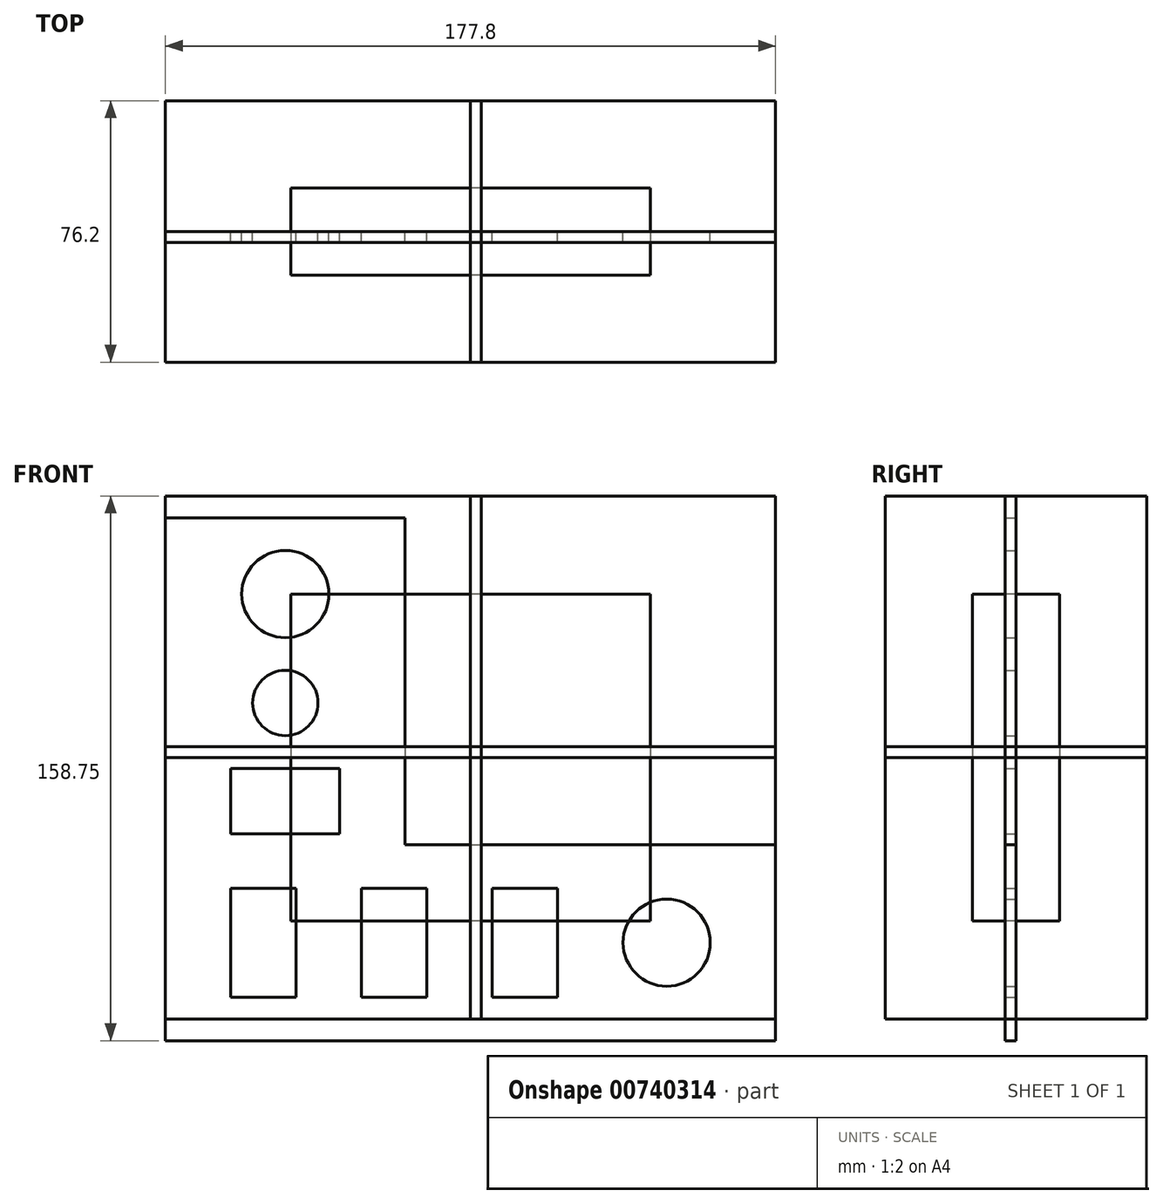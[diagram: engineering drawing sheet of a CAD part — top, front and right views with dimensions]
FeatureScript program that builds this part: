
annotation { "Feature Type Name" : "Feature", "Feature Type Description" : "" }
export const myFeature = defineFeature(function(context is Context, id is Id, definition is map)
    precondition{}
    {
        {
            var Q0;
            Q0=qCreatedBy(makeId("Front.planeOp"),FACE);
            var sketch = newSketch(context, id + "F0", { "sketchPlane" : qUnion([Q0])});
            skLineSegment(sketch, "E0.bottom", {"start": v(-19.05, 69.85) * mm, "end": v(-88.9, 69.85) * mm});
            skLineSegment(sketch, "E0.left", {"start": v(88.9, -25.4) * mm, "end": v(88.9, -69.85) * mm});
            skLineSegment(sketch, "E0.right", {"start": v(-88.9, 69.85) * mm, "end": v(-88.9, -69.85) * mm});
            skPoint(sketch, "E0.middle", {"position": v(0, 0) * mm});
            skLineSegment(sketch, "E1", {"start": v(-19.05, 69.85) * mm, "end": v(-19.05, -25.4) * mm});
            skLineSegment(sketch, "E2", {"start": v(-19.05, -25.4) * mm, "end": v(88.9, -25.4) * mm});
            skPoint(sketch, "E2.endSnap0", {"position": v(88.9, 0) * mm});
            skPoint(sketch, "E3.start.orphan", {"position": v(88.9, 69.85) * mm});
            skCircle(sketch, "E4", {"center": v(-53.98, 47.63) * mm, "radius": 12.7 * mm});
            skCircle(sketch, "E5", {"center": v(-53.98, 15.88) * mm, "radius": 9.53 * mm});
            skLineSegment(sketch, "E6.bottom", {"start": v(-38.1, -3.17) * mm, "end": v(-69.85, -3.17) * mm});
            skLineSegment(sketch, "E6.top", {"start": v(-38.1, -22.22) * mm, "end": v(-69.85, -22.22) * mm});
            skLineSegment(sketch, "E6.left", {"start": v(-38.1, -3.17) * mm, "end": v(-38.1, -22.22) * mm});
            skLineSegment(sketch, "E6.right", {"start": v(-69.85, -3.17) * mm, "end": v(-69.85, -22.22) * mm});
            skPoint(sketch, "E6.middle", {"position": v(-53.98, -12.7) * mm});
            skPoint(sketch, "E7.start.orphan", {"position": v(-53.97, 69.85) * mm});
            skLineSegment(sketch, "E8.bottom", {"start": v(-50.8, -38.1) * mm, "end": v(-69.85, -38.1) * mm});
            skLineSegment(sketch, "E8.top", {"start": v(-50.8, -69.85) * mm, "end": v(-69.85, -69.85) * mm});
            skLineSegment(sketch, "E8.left", {"start": v(-50.8, -38.1) * mm, "end": v(-50.8, -69.85) * mm});
            skLineSegment(sketch, "E8.right", {"start": v(-69.85, -38.1) * mm, "end": v(-69.85, -69.85) * mm});
            skPoint(sketch, "E8.middle", {"position": v(-60.32, -53.98) * mm});
            skLineSegment(sketch, "E9.bottom", {"start": v(-12.7, -38.1) * mm, "end": v(-31.75, -38.1) * mm});
            skLineSegment(sketch, "E9.top", {"start": v(-12.7, -69.85) * mm, "end": v(-31.75, -69.85) * mm});
            skLineSegment(sketch, "E9.left", {"start": v(-12.7, -38.1) * mm, "end": v(-12.7, -69.85) * mm});
            skLineSegment(sketch, "E9.right", {"start": v(-31.75, -38.1) * mm, "end": v(-31.75, -69.85) * mm});
            skPoint(sketch, "E9.middle", {"position": v(-22.22, -53.98) * mm});
            skLineSegment(sketch, "E10.bottom", {"start": v(25.4, -38.1) * mm, "end": v(6.35, -38.1) * mm});
            skLineSegment(sketch, "E10.top", {"start": v(25.4, -69.85) * mm, "end": v(6.35, -69.85) * mm});
            skLineSegment(sketch, "E10.left", {"start": v(25.4, -38.1) * mm, "end": v(25.4, -69.85) * mm});
            skLineSegment(sketch, "E10.right", {"start": v(6.35, -38.1) * mm, "end": v(6.35, -69.85) * mm});
            skPoint(sketch, "E10.middle", {"position": v(15.88, -53.98) * mm});
            skCircle(sketch, "E11", {"center": v(57.15, -53.98) * mm, "radius": 12.7 * mm});
            skPoint(sketch, "E12.orphan", {"position": v(88.9, -47.63) * mm});
            skLineSegment(sketch, "E13", {"start": v(88.9, -47.63) * mm, "end": v(88.9, -82.55) * mm});
            skLineSegment(sketch, "E14", {"start": v(88.9, -82.55) * mm, "end": v(-88.9, -82.55) * mm});
            skLineSegment(sketch, "E15", {"start": v(-88.9, -69.85) * mm, "end": v(-88.9, -82.55) * mm});
            skSolve(sketch);
        }
        {
            var Q0;
            Q0=qCreatedBy(makeId("Front.planeOp"),FACE);
            var sketch = newSketch(context, id + "F1", { "sketchPlane" : qUnion([Q0])});
            skLineSegment(sketch, "E16.bottom", {"start": v(52.39, 47.62) * mm, "end": v(-52.39, 47.62) * mm});
            skLineSegment(sketch, "E16.top", {"start": v(52.39, -47.63) * mm, "end": v(-52.39, -47.63) * mm});
            skLineSegment(sketch, "E16.left", {"start": v(52.39, 47.62) * mm, "end": v(52.39, -47.63) * mm});
            skLineSegment(sketch, "E16.right", {"start": v(-52.39, 47.62) * mm, "end": v(-52.39, -47.63) * mm});
            skPoint(sketch, "E16.middle", {"position": v(0, 0) * mm});
            skSolve(sketch);
        }
        {
            var Q0;
            Q0=qCreatedBy(makeId("Right.planeOp"),FACE);
            var sketch = newSketch(context, id + "F2", { "sketchPlane" : qUnion([Q0])});
            skLineSegment(sketch, "E17.bottom", {"start": v(38.1, 76.2) * mm, "end": v(-38.1, 76.2) * mm});
            skLineSegment(sketch, "E17.top", {"start": v(38.1, -76.2) * mm, "end": v(-38.1, -76.2) * mm});
            skLineSegment(sketch, "E17.left", {"start": v(38.1, 76.2) * mm, "end": v(38.1, -76.2) * mm});
            skLineSegment(sketch, "E17.right", {"start": v(-38.1, 76.2) * mm, "end": v(-38.1, -76.2) * mm});
            skPoint(sketch, "E17.middle", {"position": v(0, 0) * mm});
            skSolve(sketch);
        }
        {
            var Q0;
            Q0=qCreatedBy(makeId("Top.planeOp"),FACE);
            var sketch = newSketch(context, id + "F3", { "sketchPlane" : qUnion([Q0])});
            skLineSegment(sketch, "E18.bottom", {"start": v(88.9, 38.1) * mm, "end": v(-88.9, 38.1) * mm});
            skLineSegment(sketch, "E18.top", {"start": v(88.9, -38.1) * mm, "end": v(-88.9, -38.1) * mm});
            skLineSegment(sketch, "E18.left", {"start": v(88.9, 38.1) * mm, "end": v(88.9, -38.1) * mm});
            skLineSegment(sketch, "E18.right", {"start": v(-88.9, 38.1) * mm, "end": v(-88.9, -38.1) * mm});
            skPoint(sketch, "E18.middle", {"position": v(0, 0) * mm});
            skSolve(sketch);
        }
        {
            var Q0;
            Q0=qCreatedBy(makeId("Front.planeOp"),FACE);
            var sketch = newSketch(context, id + "F4", { "sketchPlane" : qUnion([Q0])});
            skLineSegment(sketch, "E19.bottom", {"start": v(88.9, 76.2) * mm, "end": v(-88.9, 76.2) * mm});
            skLineSegment(sketch, "E19.top", {"start": v(88.9, -76.2) * mm, "end": v(-88.9, -76.2) * mm});
            skLineSegment(sketch, "E19.left", {"start": v(88.9, 76.2) * mm, "end": v(88.9, -76.2) * mm});
            skLineSegment(sketch, "E19.right", {"start": v(-88.9, 76.2) * mm, "end": v(-88.9, -76.2) * mm});
            skPoint(sketch, "E19.middle", {"position": v(0, 0) * mm});
            skSolve(sketch);
        }
        {
            var Q0;
            Q0 = qSketchRegion(id + "F0", true);
            extrude(context, id + "F5", {"entities" : qUnion([Q0]), "depth" : 3.17 * mm, "offsetDistance" : 25.4 * mm});
        }
        {
            var Q0;
            Q0 = qSketchRegion(id + "F1", true);
            extrude(context, id + "F6", {"entities" : qUnion([Q0]), "depth" : 3.17 * mm, "offsetDistance" : 25.4 * mm});
        }
        {
            var Q0;
            Q0 = qSketchRegion(id + "F2", true);
            extrude(context, id + "F7", {"entities" : qUnion([Q0]), "depth" : 3.17 * mm, "offsetDistance" : 25.4 * mm});
        }
        {
            var Q0;
            Q0 = qSketchRegion(id + "F3", true);
            extrude(context, id + "F8", {"entities" : qUnion([Q0]), "depth" : 3.17 * mm, "offsetDistance" : 25.4 * mm});
        }
        {
            var Q0;
            Q0 = qSketchRegion(id + "F4", true);
            extrude(context, id + "F9", {"entities" : qUnion([Q0]), "depth" : 3.17 * mm, "offsetDistance" : 25.4 * mm});
        }
        {
            var Q0;
            Q0=qCreatedBy(makeId("Right.planeOp"),FACE);
            var sketch = newSketch(context, id + "F10", { "sketchPlane" : qUnion([Q0])});
            skLineSegment(sketch, "E20.bottom", {"start": v(12.7, 47.63) * mm, "end": v(-12.7, 47.63) * mm});
            skLineSegment(sketch, "E20.top", {"start": v(12.7, -47.62) * mm, "end": v(-12.7, -47.62) * mm});
            skLineSegment(sketch, "E20.left", {"start": v(12.7, 47.63) * mm, "end": v(12.7, -47.62) * mm});
            skLineSegment(sketch, "E20.right", {"start": v(-12.7, 47.63) * mm, "end": v(-12.7, -47.62) * mm});
            skPoint(sketch, "E20.middle", {"position": v(0, 0) * mm});
            skSolve(sketch);
        }
        {
            var Q0;
            Q0 = qSketchRegion(id + "F10", true);
            extrude(context, id + "F11", {"entities" : qUnion([Q0]), "depth" : 3.17 * mm, "offsetDistance" : 25.4 * mm});
        }
        {
            var Q0;
            Q0=qCreatedBy(makeId("Top.planeOp"),FACE);
            var sketch = newSketch(context, id + "F12", { "sketchPlane" : qUnion([Q0])});
            skLineSegment(sketch, "E21.bottom", {"start": v(52.39, 12.7) * mm, "end": v(-52.39, 12.7) * mm});
            skLineSegment(sketch, "E21.top", {"start": v(52.39, -12.7) * mm, "end": v(-52.39, -12.7) * mm});
            skLineSegment(sketch, "E21.left", {"start": v(52.39, 12.7) * mm, "end": v(52.39, -12.7) * mm});
            skLineSegment(sketch, "E21.right", {"start": v(-52.39, 12.7) * mm, "end": v(-52.39, -12.7) * mm});
            skPoint(sketch, "E21.middle", {"position": v(0, 0) * mm});
            skSolve(sketch);
        }
        {
            var Q0;
            Q0 = qSketchRegion(id + "F12", true);
            extrude(context, id + "F13", {"entities" : qUnion([Q0]), "depth" : 3.17 * mm, "offsetDistance" : 25.4 * mm});
        }
    });
